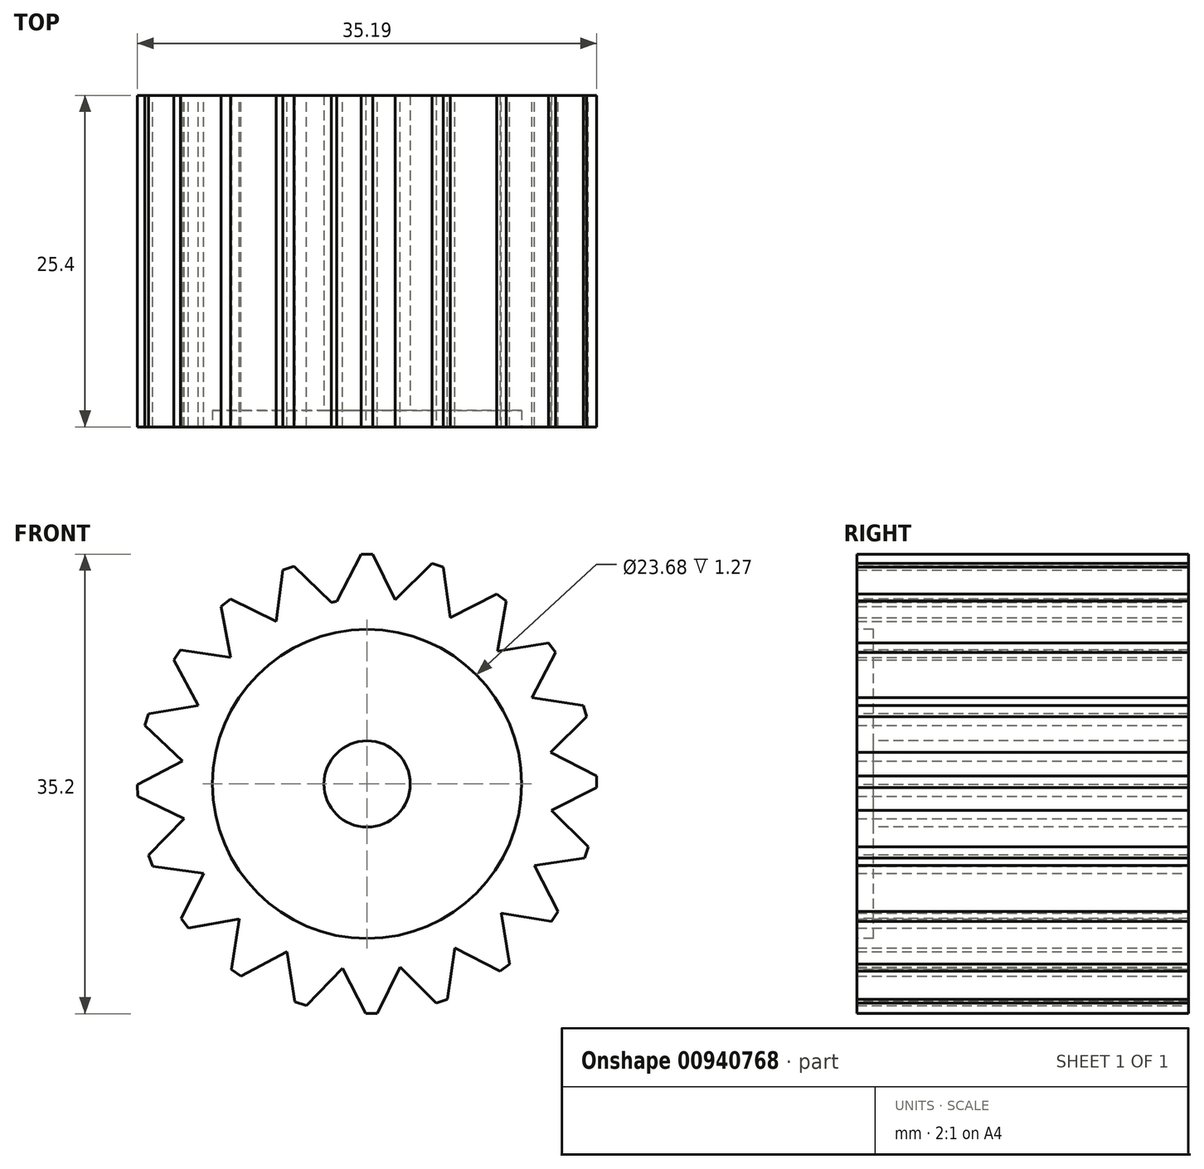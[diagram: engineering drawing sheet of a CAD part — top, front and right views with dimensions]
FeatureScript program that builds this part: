
annotation { "Feature Type Name" : "Feature", "Feature Type Description" : "" }
export const myFeature = defineFeature(function(context is Context, id is Id, definition is map)
    precondition{}
    {
        {
            var Q0;
            Q0=qCreatedBy(makeId("Front.planeOp"),FACE);
            var sketch = newSketch(context, id + "F0", { "sketchPlane" : qUnion([Q0])});
            skCircle(sketch, "E0", {"center": v(0, 0) * mm, "radius": 14.18 * mm});
            skLineSegment(sketch, "E1", {"start": v(-2.33, 13.98) * mm, "end": v(0, 18.5) * mm});
            skLineSegment(sketch, "E2", {"start": v(0, 18.5) * mm, "end": v(2.49, 13.4) * mm});
            skLineSegment(sketch, "E3.1.0", {"start": v(5.68, 17.6) * mm, "end": v(6.49, 12) * mm});
            skLineSegment(sketch, "E3.1.1", {"start": v(2.08, 14.02) * mm, "end": v(5.68, 17.6) * mm});
            skLineSegment(sketch, "E3.2.0", {"start": v(10.82, 15) * mm, "end": v(9.86, 9.42) * mm});
            skLineSegment(sketch, "E3.2.1", {"start": v(6.3, 12.7) * mm, "end": v(10.82, 15) * mm});
            skLineSegment(sketch, "E3.3.0", {"start": v(14.9, 10.96) * mm, "end": v(12.28, 5.93) * mm});
            skLineSegment(sketch, "E3.3.1", {"start": v(9.89, 10.16) * mm, "end": v(14.9, 10.96) * mm});
            skLineSegment(sketch, "E3.4.0", {"start": v(17.55, 5.85) * mm, "end": v(13.5, 1.88) * mm});
            skLineSegment(sketch, "E3.4.1", {"start": v(12.53, 6.63) * mm, "end": v(17.55, 5.85) * mm});
            skLineSegment(sketch, "E3.5.0", {"start": v(18.5, 0.17) * mm, "end": v(13.43, -2.36) * mm});
            skLineSegment(sketch, "E3.5.1", {"start": v(13.96, 2.46) * mm, "end": v(18.5, 0.17) * mm});
            skLineSegment(sketch, "E3.6.0", {"start": v(17.66, -5.52) * mm, "end": v(12.05, -6.38) * mm});
            skLineSegment(sketch, "E3.6.1", {"start": v(14.04, -1.95) * mm, "end": v(17.66, -5.52) * mm});
            skLineSegment(sketch, "E3.7.0", {"start": v(15.1, -10.68) * mm, "end": v(9.5, -9.77) * mm});
            skLineSegment(sketch, "E3.7.1", {"start": v(12.76, -6.17) * mm, "end": v(15.1, -10.68) * mm});
            skLineSegment(sketch, "E3.8.0", {"start": v(11.1, -14.8) * mm, "end": v(6.05, -12.22) * mm});
            skLineSegment(sketch, "E3.8.1", {"start": v(10.25, -9.8) * mm, "end": v(11.1, -14.8) * mm});
            skLineSegment(sketch, "E3.9.0", {"start": v(6, -17.5) * mm, "end": v(2, -13.49) * mm});
            skLineSegment(sketch, "E3.9.1", {"start": v(6.74, -12.47) * mm, "end": v(6, -17.5) * mm});
            skLineSegment(sketch, "E3.10.0", {"start": v(0.34, -18.5) * mm, "end": v(-2.24, -13.45) * mm});
            skLineSegment(sketch, "E3.10.1", {"start": v(2.58, -13.94) * mm, "end": v(0.34, -18.5) * mm});
            skLineSegment(sketch, "E3.11.0", {"start": v(-5.36, -17.7) * mm, "end": v(-6.27, -12.11) * mm});
            skLineSegment(sketch, "E3.11.1", {"start": v(-1.82, -14.06) * mm, "end": v(-5.36, -17.7) * mm});
            skLineSegment(sketch, "E3.12.0", {"start": v(-10.54, -15.2) * mm, "end": v(-9.68, -9.6) * mm});
            skLineSegment(sketch, "E3.12.1", {"start": v(-6.06, -12.82) * mm, "end": v(-10.54, -15.2) * mm});
            skLineSegment(sketch, "E3.13.0", {"start": v(-14.7, -11.23) * mm, "end": v(-12.16, -6.16) * mm});
            skLineSegment(sketch, "E3.13.1", {"start": v(-9.7, -10.34) * mm, "end": v(-14.7, -11.23) * mm});
            skLineSegment(sketch, "E3.14.0", {"start": v(-17.44, -6.17) * mm, "end": v(-13.47, -2.12) * mm});
            skLineSegment(sketch, "E3.14.1", {"start": v(-12.4, -6.86) * mm, "end": v(-17.44, -6.17) * mm});
            skLineSegment(sketch, "E3.15.0", {"start": v(-18.5, -0.5) * mm, "end": v(-13.47, 2.12) * mm});
            skLineSegment(sketch, "E3.15.1", {"start": v(-13.91, -2.71) * mm, "end": v(-18.5, -0.5) * mm});
            skLineSegment(sketch, "E3.16.0", {"start": v(-17.75, 5.2) * mm, "end": v(-12.17, 6.15) * mm});
            skLineSegment(sketch, "E3.16.1", {"start": v(-14.07, 1.7) * mm, "end": v(-17.75, 5.2) * mm});
            skLineSegment(sketch, "E3.17.0", {"start": v(-15.3, 10.4) * mm, "end": v(-9.69, 9.6) * mm});
            skLineSegment(sketch, "E3.17.1", {"start": v(-12.87, 5.94) * mm, "end": v(-15.3, 10.4) * mm});
            skLineSegment(sketch, "E3.18.0", {"start": v(-11.36, 14.6) * mm, "end": v(-6.27, 12.1) * mm});
            skLineSegment(sketch, "E3.18.1", {"start": v(-10.43, 9.6) * mm, "end": v(-11.36, 14.6) * mm});
            skLineSegment(sketch, "E3.19.0", {"start": v(-6.33, 17.38) * mm, "end": v(-2.25, 13.45) * mm});
            skLineSegment(sketch, "E3.19.1", {"start": v(-6.97, 12.34) * mm, "end": v(-6.33, 17.38) * mm});
            skLineSegment(sketch, "E3.anchor1", {"start": v(0, 0) * mm, "end": v(2.49, 13.4) * mm, "construction": true});
            skLineSegment(sketch, "E3.anchor2", {"start": v(0, 0) * mm, "end": v(-2.25, 13.45) * mm, "construction": true});
            skSolve(sketch);
        }
        {
            var Q0;
            Q0 = qSketchRegion(id + "F0", true);
            extrude(context, id + "F1", {"entities" : qUnion([Q0]), "depth" : 25.4 * mm, "offsetDistance" : 25.4 * mm});
        }
        {
            var Q0;
            Q0=makeQuery(id+"F1.opExtrude","SWEPT_EDGE",EDGE,{"disambiguationData":[OSD([sQuery(id+"F0.wireOp",EDGE,"E1"),sQuery(id+"F0.wireOp",EDGE,"E2")])]});
            var Q1;
            Q1=makeQuery(id+"F1.opExtrude","SWEPT_EDGE",EDGE,{"disambiguationData":[OSD([sQuery(id+"F0.wireOp",EDGE,"E3.1.0"),sQuery(id+"F0.wireOp",EDGE,"E3.1.1")])]});
            var Q2;
            Q2=makeQuery(id+"F1.opExtrude","SWEPT_EDGE",EDGE,{"disambiguationData":[OSD([sQuery(id+"F0.wireOp",EDGE,"E3.2.0"),sQuery(id+"F0.wireOp",EDGE,"E3.2.1")])]});
            var Q3;
            Q3=makeQuery(id+"F1.opExtrude","SWEPT_EDGE",EDGE,{"disambiguationData":[OSD([sQuery(id+"F0.wireOp",EDGE,"E3.3.0"),sQuery(id+"F0.wireOp",EDGE,"E3.3.1")])]});
            var Q4;
            Q4=makeQuery(id+"F1.opExtrude","SWEPT_EDGE",EDGE,{"disambiguationData":[OSD([sQuery(id+"F0.wireOp",EDGE,"E3.4.0"),sQuery(id+"F0.wireOp",EDGE,"E3.4.1")])]});
            var Q5;
            Q5=makeQuery(id+"F1.opExtrude","SWEPT_EDGE",EDGE,{"disambiguationData":[OSD([sQuery(id+"F0.wireOp",EDGE,"E3.5.0"),sQuery(id+"F0.wireOp",EDGE,"E3.5.1")])]});
            var Q6;
            Q6=makeQuery(id+"F1.opExtrude","SWEPT_EDGE",EDGE,{"disambiguationData":[OSD([sQuery(id+"F0.wireOp",EDGE,"E3.6.0"),sQuery(id+"F0.wireOp",EDGE,"E3.6.1")])]});
            var Q7;
            Q7=makeQuery(id+"F1.opExtrude","SWEPT_EDGE",EDGE,{"disambiguationData":[OSD([sQuery(id+"F0.wireOp",EDGE,"E3.7.0"),sQuery(id+"F0.wireOp",EDGE,"E3.7.1")])]});
            var Q8;
            Q8=makeQuery(id+"F1.opExtrude","SWEPT_EDGE",EDGE,{"disambiguationData":[OSD([sQuery(id+"F0.wireOp",EDGE,"E3.8.0"),sQuery(id+"F0.wireOp",EDGE,"E3.8.1")])]});
            var Q9;
            Q9=makeQuery(id+"F1.opExtrude","SWEPT_EDGE",EDGE,{"disambiguationData":[OSD([sQuery(id+"F0.wireOp",EDGE,"E3.9.0"),sQuery(id+"F0.wireOp",EDGE,"E3.9.1")])]});
            var Q10;
            Q10=makeQuery(id+"F1.opExtrude","SWEPT_EDGE",EDGE,{"disambiguationData":[OSD([sQuery(id+"F0.wireOp",EDGE,"E3.10.0"),sQuery(id+"F0.wireOp",EDGE,"E3.10.1")])]});
            var Q11;
            Q11=makeQuery(id+"F1.opExtrude","SWEPT_EDGE",EDGE,{"disambiguationData":[OSD([sQuery(id+"F0.wireOp",EDGE,"E3.11.0"),sQuery(id+"F0.wireOp",EDGE,"E3.11.1")])]});
            var Q12;
            Q12=makeQuery(id+"F1.opExtrude","SWEPT_EDGE",EDGE,{"disambiguationData":[OSD([sQuery(id+"F0.wireOp",EDGE,"E3.12.0"),sQuery(id+"F0.wireOp",EDGE,"E3.12.1")])]});
            var Q13;
            Q13=makeQuery(id+"F1.opExtrude","SWEPT_EDGE",EDGE,{"disambiguationData":[OSD([sQuery(id+"F0.wireOp",EDGE,"E3.13.0"),sQuery(id+"F0.wireOp",EDGE,"E3.13.1")])]});
            var Q14;
            Q14=makeQuery(id+"F1.opExtrude","SWEPT_EDGE",EDGE,{"disambiguationData":[OSD([sQuery(id+"F0.wireOp",EDGE,"E3.14.0"),sQuery(id+"F0.wireOp",EDGE,"E3.14.1")])]});
            var Q15;
            Q15=makeQuery(id+"F1.opExtrude","SWEPT_EDGE",EDGE,{"disambiguationData":[OSD([sQuery(id+"F0.wireOp",EDGE,"E3.15.0"),sQuery(id+"F0.wireOp",EDGE,"E3.15.1")])]});
            var Q16;
            Q16=makeQuery(id+"F1.opExtrude","SWEPT_EDGE",EDGE,{"disambiguationData":[OSD([sQuery(id+"F0.wireOp",EDGE,"E3.16.0"),sQuery(id+"F0.wireOp",EDGE,"E3.16.1")])]});
            var Q17;
            Q17=makeQuery(id+"F1.opExtrude","SWEPT_EDGE",EDGE,{"disambiguationData":[OSD([sQuery(id+"F0.wireOp",EDGE,"E3.17.0"),sQuery(id+"F0.wireOp",EDGE,"E3.17.1")])]});
            var Q18;
            Q18=makeQuery(id+"F1.opExtrude","SWEPT_EDGE",EDGE,{"disambiguationData":[OSD([sQuery(id+"F0.wireOp",EDGE,"E3.18.0"),sQuery(id+"F0.wireOp",EDGE,"E3.18.1")])]});
            var Q19;
            Q19=makeQuery(id+"F1.opExtrude","SWEPT_EDGE",EDGE,{"disambiguationData":[OSD([sQuery(id+"F0.wireOp",EDGE,"E3.19.0"),sQuery(id+"F0.wireOp",EDGE,"E3.19.1")])]});
            chamfer(context, id + "F2", {"entities" : qUnion([Q0, Q1, Q2, Q3, Q4, Q5, Q6, Q7, Q8, Q9, Q10, Q11, Q12, Q13, Q14, Q15, Q16, Q17, Q18, Q19]), "width" : 0.5 * mm, "tangentPropagation" : true});
        }
        {
            var Q0;
            Q0=makeQuery(id+"F1.opExtrude","CAP_FACE",FACE,{"disambiguationData":[OSD([sQuery(id+"F0.wireOp",EDGE,"E0"),sQuery(id+"F0.wireOp",EDGE,"E1"),sQuery(id+"F0.wireOp",EDGE,"E2"),sQuery(id+"F0.wireOp",EDGE,"E3.1.0"),sQuery(id+"F0.wireOp",EDGE,"E3.1.1"),sQuery(id+"F0.wireOp",EDGE,"E3.2.0"),sQuery(id+"F0.wireOp",EDGE,"E3.2.1"),sQuery(id+"F0.wireOp",EDGE,"E3.3.0"),sQuery(id+"F0.wireOp",EDGE,"E3.3.1"),sQuery(id+"F0.wireOp",EDGE,"E3.4.0"),sQuery(id+"F0.wireOp",EDGE,"E3.4.1"),sQuery(id+"F0.wireOp",EDGE,"E3.5.0"),sQuery(id+"F0.wireOp",EDGE,"E3.5.1"),sQuery(id+"F0.wireOp",EDGE,"E3.6.0"),sQuery(id+"F0.wireOp",EDGE,"E3.6.1"),sQuery(id+"F0.wireOp",EDGE,"E3.7.0"),sQuery(id+"F0.wireOp",EDGE,"E3.7.1"),sQuery(id+"F0.wireOp",EDGE,"E3.8.0"),sQuery(id+"F0.wireOp",EDGE,"E3.8.1"),sQuery(id+"F0.wireOp",EDGE,"E3.9.0"),sQuery(id+"F0.wireOp",EDGE,"E3.9.1"),sQuery(id+"F0.wireOp",EDGE,"E3.10.0"),sQuery(id+"F0.wireOp",EDGE,"E3.10.1"),sQuery(id+"F0.wireOp",EDGE,"E3.11.0"),sQuery(id+"F0.wireOp",EDGE,"E3.11.1"),sQuery(id+"F0.wireOp",EDGE,"E3.12.0"),sQuery(id+"F0.wireOp",EDGE,"E3.12.1"),sQuery(id+"F0.wireOp",EDGE,"E3.13.0"),sQuery(id+"F0.wireOp",EDGE,"E3.13.1"),sQuery(id+"F0.wireOp",EDGE,"E3.14.0"),sQuery(id+"F0.wireOp",EDGE,"E3.14.1"),sQuery(id+"F0.wireOp",EDGE,"E3.15.0"),sQuery(id+"F0.wireOp",EDGE,"E3.15.1"),sQuery(id+"F0.wireOp",EDGE,"E3.16.0"),sQuery(id+"F0.wireOp",EDGE,"E3.16.1"),sQuery(id+"F0.wireOp",EDGE,"E3.17.0"),sQuery(id+"F0.wireOp",EDGE,"E3.17.1"),sQuery(id+"F0.wireOp",EDGE,"E3.18.0"),sQuery(id+"F0.wireOp",EDGE,"E3.18.1"),sQuery(id+"F0.wireOp",EDGE,"E3.19.0"),sQuery(id+"F0.wireOp",EDGE,"E3.19.1")])],"isStart":false});
            var sketch = newSketch(context, id + "F3", { "sketchPlane" : qUnion([Q0])});
            skCircle(sketch, "E4", {"center": v(0, 0) * mm, "radius": 3.3 * mm});
            skSolve(sketch);
        }
        {
            var Q0;
            Q0=makeQuery(id+"F3.imprint","IMPRINT",FACE,{"disambiguationData":[TD([[makeQuery(id+"F3.imprint","IMPRINT",EDGE,{"derivedFrom":sQuery(id+"F3.wireOp",EDGE,"E4")}),1.0]])]});
            extrude(context, id + "F4", {"entities" : qUnion([Q0]), "operationType" : NewBodyOperationType.REMOVE, "endBound" : BoundingType.THROUGH_ALL, "oppositeDirection" : true, "depth" : 25.4 * mm, "offsetDistance" : 25.4 * mm});
        }
        {
            var Q0;
            Q0=makeQuery(id+"F1.opExtrude","CAP_FACE",FACE,{"disambiguationData":[OSD([sQuery(id+"F0.wireOp",EDGE,"E0"),sQuery(id+"F0.wireOp",EDGE,"E1"),sQuery(id+"F0.wireOp",EDGE,"E2"),sQuery(id+"F0.wireOp",EDGE,"E3.1.0"),sQuery(id+"F0.wireOp",EDGE,"E3.1.1"),sQuery(id+"F0.wireOp",EDGE,"E3.2.0"),sQuery(id+"F0.wireOp",EDGE,"E3.2.1"),sQuery(id+"F0.wireOp",EDGE,"E3.3.0"),sQuery(id+"F0.wireOp",EDGE,"E3.3.1"),sQuery(id+"F0.wireOp",EDGE,"E3.4.0"),sQuery(id+"F0.wireOp",EDGE,"E3.4.1"),sQuery(id+"F0.wireOp",EDGE,"E3.5.0"),sQuery(id+"F0.wireOp",EDGE,"E3.5.1"),sQuery(id+"F0.wireOp",EDGE,"E3.6.0"),sQuery(id+"F0.wireOp",EDGE,"E3.6.1"),sQuery(id+"F0.wireOp",EDGE,"E3.7.0"),sQuery(id+"F0.wireOp",EDGE,"E3.7.1"),sQuery(id+"F0.wireOp",EDGE,"E3.8.0"),sQuery(id+"F0.wireOp",EDGE,"E3.8.1"),sQuery(id+"F0.wireOp",EDGE,"E3.9.0"),sQuery(id+"F0.wireOp",EDGE,"E3.9.1"),sQuery(id+"F0.wireOp",EDGE,"E3.10.0"),sQuery(id+"F0.wireOp",EDGE,"E3.10.1"),sQuery(id+"F0.wireOp",EDGE,"E3.11.0"),sQuery(id+"F0.wireOp",EDGE,"E3.11.1"),sQuery(id+"F0.wireOp",EDGE,"E3.12.0"),sQuery(id+"F0.wireOp",EDGE,"E3.12.1"),sQuery(id+"F0.wireOp",EDGE,"E3.13.0"),sQuery(id+"F0.wireOp",EDGE,"E3.13.1"),sQuery(id+"F0.wireOp",EDGE,"E3.14.0"),sQuery(id+"F0.wireOp",EDGE,"E3.14.1"),sQuery(id+"F0.wireOp",EDGE,"E3.15.0"),sQuery(id+"F0.wireOp",EDGE,"E3.15.1"),sQuery(id+"F0.wireOp",EDGE,"E3.16.0"),sQuery(id+"F0.wireOp",EDGE,"E3.16.1"),sQuery(id+"F0.wireOp",EDGE,"E3.17.0"),sQuery(id+"F0.wireOp",EDGE,"E3.17.1"),sQuery(id+"F0.wireOp",EDGE,"E3.18.0"),sQuery(id+"F0.wireOp",EDGE,"E3.18.1"),sQuery(id+"F0.wireOp",EDGE,"E3.19.0"),sQuery(id+"F0.wireOp",EDGE,"E3.19.1")])],"isStart":false});
            var sketch = newSketch(context, id + "F5", { "sketchPlane" : qUnion([Q0])});
            skCircle(sketch, "E5", {"center": v(0, 0) * mm, "radius": 11.84 * mm});
            skSolve(sketch);
        }
        {
            var Q0;
            Q0 = qSketchRegion(id + "F5", true);
            extrude(context, id + "F6", {"entities" : qUnion([Q0]), "operationType" : NewBodyOperationType.REMOVE, "oppositeDirection" : true, "depth" : 1.27 * mm, "offsetDistance" : 25.4 * mm});
        }
        {
            var Q0;
            Q0=makeQuery(id+"F1.opExtrude","SWEPT_EDGE",EDGE,{"disambiguationData":[OSD([sQuery(id+"F0.wireOp",EDGE,"E3.17.0"),sQuery(id+"F0.wireOp",EDGE,"E3.18.1")])]});
            cPoint(context, id + "F7", {"entities" : qUnion([Q0]), "parameter" : 0.5});
        }
        {
            var Q0;
            Q0=qCreatedBy(makeId("Front.planeOp"),FACE);
            var Q1;
            Q1 = qCreatedBy(id + "F7" ,VERTEX);
            cPlane(context, id + "F8", {"entities" : qUnion([Q0, Q1]), "cplaneType" : CPlaneType.PLANE_POINT, "offset" : 25.4 * mm, "width" : 152.4 * mm, "height" : 152.4 * mm});
        }
    });
